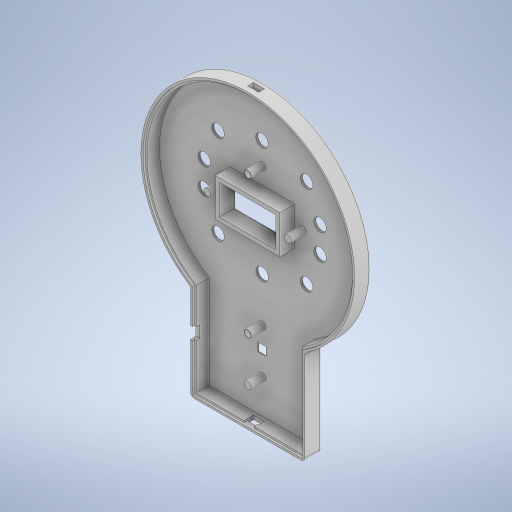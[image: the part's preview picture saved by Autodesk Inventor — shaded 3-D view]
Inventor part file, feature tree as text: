
AUTODESK INVENTOR PART (.ipt)
format: ipt  version: 2024 (Build 280153000, 153)  size: 580,096 bytes
history: native  units: mm
features: sketch x17, extrude x16, fillet x4, other x1
ambient origin geometry x8: Origin, YZ Plane, XZ Plane, XY Plane, X Axis, Y Axis, Z Axis, Center Point
bodies: Body1 (feature_tree)
feature tree (38):
  extrude  "Extrusion2"  Depth=102.0mm
  sketch  "Esquisse2"
  extrude  "Extrusion5"  Depth=26.4mm
  sketch  "Esquisse4"
  sketch  "Esquisse5"
  extrude  "Extrusion6"  Depth=90.0mm
  extrude  "Extrusion7"  Depth=26.4mm
  extrude  "Extrusion8"  Depth=1.0mm TaperAngle=0.0deg
  extrude  "Extrusion9"  Depth=3.5mm
  fillet  "Congé1"  Radius=39.1mm
  fillet  "Congé2"  Radius=26.4mm
  extrude  "Extrusion10"  Depth=3.5mm
  sketch  "Esquisse10"
  extrude  "Extrusion11"  Depth=107.68mm
  extrude  "Extrusion12"  Depth=26.4mm
  fillet  "Congé3"  Radius=7.195mm
  extrude  "Extrusion13"  Depth=3.0mm
  extrude  "Extrusion14"  Depth=3.0mm
  sketch  "Esquisse18"
  other  "Plan de construction7"
  extrude  "Extrusion16"  Depth=3.0mm TaperAngle=0.0deg
  extrude  "Extrusion17"  Depth=3.0mm TaperAngle=0.0deg
  extrude  "Extrusion18"  Depth=3.5mm
  fillet  "Congé4"  Radius=17.0mm
  extrude  "Extrusion19"  Depth=3.5mm
  extrude  "Extrusion20"  Depth=3.5mm
  sketch  "Esquisse1"
  sketch  "Esquisse6"
  sketch  "Esquisse8"
  sketch  "Esquisse9"
  sketch  "Esquisse11"
  sketch  "Esquisse12"
  sketch  "Esquisse13"
  sketch  "Esquisse14"
  sketch  "Esquisse19"
  sketch  "Esquisse20"
  sketch  "Esquisse21"
  sketch  "Esquisse22"
